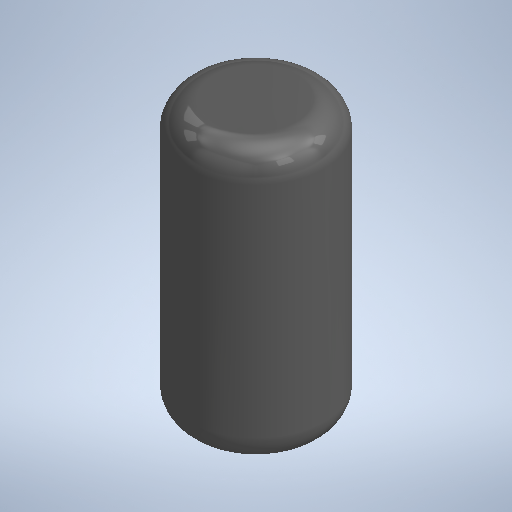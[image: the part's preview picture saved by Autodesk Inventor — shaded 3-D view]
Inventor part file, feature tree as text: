
AUTODESK INVENTOR PART (.ipt)
format: ipt  version: 2025.1 (Build 291241020, 241B)  size: 224,256 bytes
history: native  units: mm (DEFAULTED — no unit token found)
features: extrude x1, fillet x1, sketch x1
ambient origin geometry x8: Origin, YZ Plane, XZ Plane, XY Plane, X Axis, Y Axis, Z Axis, Center Point
bodies: Solid1 (feature_tree)
feature tree (3):
  extrude  "Extrusion1"  Depth=5.0mm TaperAngle=0.0deg
  fillet  "Fillet1"  Radius=0.5mm
  sketch  "Sketch1"  dims[d0=2.49mm d1=5.0mm d2=0.0mm d3=0.5mm]
